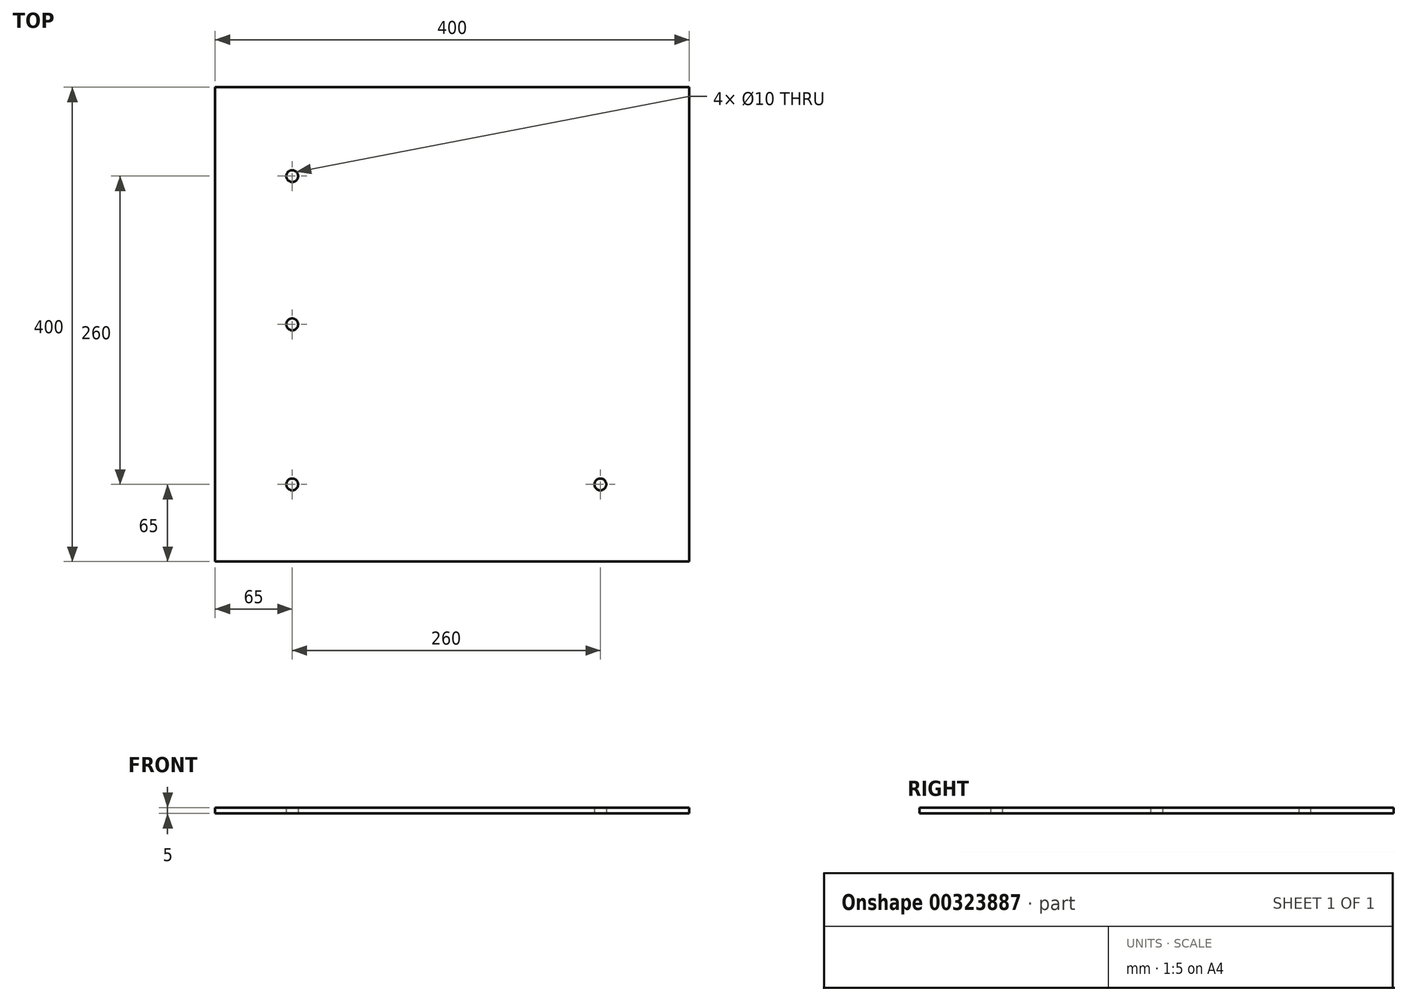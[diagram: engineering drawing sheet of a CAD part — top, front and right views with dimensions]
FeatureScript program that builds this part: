
annotation { "Feature Type Name" : "Feature", "Feature Type Description" : "" }
export const myFeature = defineFeature(function(context is Context, id is Id, definition is map)
    precondition{}
    {
        {
            var Q0;
            Q0=qCreatedBy(makeId("Top.planeOp"),FACE);
            var sketch = newSketch(context, id + "F0", { "sketchPlane" : qUnion([Q0])});
            skLineSegment(sketch, "E0.bottom", {"start": v(-200, 200) * mm, "end": v(200, 200) * mm});
            skLineSegment(sketch, "E0.right", {"start": v(200, 200) * mm, "end": v(200, -200) * mm});
            skLineSegment(sketch, "E1", {"start": v(-200, 200) * mm, "end": v(-200, -200) * mm});
            skLineSegment(sketch, "E2", {"start": v(-200, -200) * mm, "end": v(-200, -70) * mm});
            skLineSegment(sketch, "E3", {"start": v(-200, -70) * mm, "end": v(-200, 60) * mm});
            skLineSegment(sketch, "E4", {"start": v(-200, 60) * mm, "end": v(-200, 190) * mm});
            skLineSegment(sketch, "E5", {"start": v(60, -200) * mm, "end": v(60, 190) * mm});
            skLineSegment(sketch, "E6", {"start": v(60, 190) * mm, "end": v(-200, 190) * mm});
            skLineSegment(sketch, "E7", {"start": v(-200, -70) * mm, "end": v(60, -70) * mm});
            skLineSegment(sketch, "E8", {"start": v(-200, 60) * mm, "end": v(60, 60) * mm});
            skLineSegment(sketch, "E9", {"start": v(60, -200) * mm, "end": v(190, -200) * mm});
            skLineSegment(sketch, "E10", {"start": v(190, -200) * mm, "end": v(190, 60) * mm});
            skLineSegment(sketch, "E11", {"start": v(190, 60) * mm, "end": v(60, 60) * mm});
            skLineSegment(sketch, "E12", {"start": v(190, 60) * mm, "end": v(190, 180) * mm});
            skLineSegment(sketch, "E13", {"start": v(190, 180) * mm, "end": v(60, 180) * mm});
            skCircle(sketch, "E14", {"center": v(-135, -135) * mm, "radius": 5 * mm});
            skLineSegment(sketch, "E15", {"start": v(60, -200) * mm, "end": v(-200, -200) * mm});
            skCircle(sketch, "E16", {"center": v(-135, 0) * mm, "radius": 5 * mm});
            skCircle(sketch, "E17", {"center": v(-135, 125) * mm, "radius": 5 * mm});
            skCircle(sketch, "E18", {"center": v(125, -135) * mm, "radius": 5 * mm});
            skLineSegment(sketch, "E19", {"start": v(190, -200) * mm, "end": v(200, -200) * mm});
            skSolve(sketch);
        }
        {
            var Q0;
            Q0=qSketchRegion(id+"F0",true);
            extrude(context, id + "F1", {"entities" : qUnion([Q0]), "depth" : 5 * mm});
        }
        {
            var Q0;
            {var subQ0=sQuery(id+"F0.wireOp",EDGE,"E11");Q0=makeQuery(id+"F0.imprint","IMPRINT",FACE,{"disambiguationData":[TD([[makeQuery(id+"F0.imprint","IMPRINT",EDGE,{"derivedFrom":subQ0}),-1.0]])]});}
            extrude(context, id + "F2", {"entities" : qUnion([Q0]), "operationType" : NewBodyOperationType.ADD, "depth" : 5 * mm});
        }
    });
